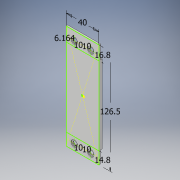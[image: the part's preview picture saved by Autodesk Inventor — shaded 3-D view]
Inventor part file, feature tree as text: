
AUTODESK INVENTOR PART (.ipt)
format: ipt  version: 2018 (Build 220112000, 112)  size: 128,000 bytes
history: native  units: in
note: dims shown in document units (in); Inventor stores cm internally (conversion verified against a paired STEP export)
features: extrude x2, sketch x1, hole x1
ambient origin geometry x8: Origin, YZ Plane, XZ Plane, XY Plane, X Axis, Y Axis, Z Axis, Center Point
bodies: Solid1 (feature_tree)
feature tree (4):
  sketch  "Sketch1"  dims[d0=1.5748in d1=4.9803in d2=0.0787in d3=0.0in d4=0.5827in d5=0.3937in d6=0.3937in d9=0.6614in d10=0.2427in d11=0.3937in d12=0.3937in d13=0.1575in d14=0.0in d15=0.1969in d16=0.2362in d17=0.315in d18=0.0394in d19=90.0deg d20=0.315in d21=0.8108in]
  extrude  "Extrusion1"  Depth=4.9803in
  extrude  "Extrusion2"  Depth=0.0787in TaperAngle=0.0deg
  hole  "Hole1"  [1 undecoded]
note: 1 required parameter value undecoded (feature->parameter linkage not recoverable at this tier; creation-order binding heuristic only, values carry confidence <= 0.55)
